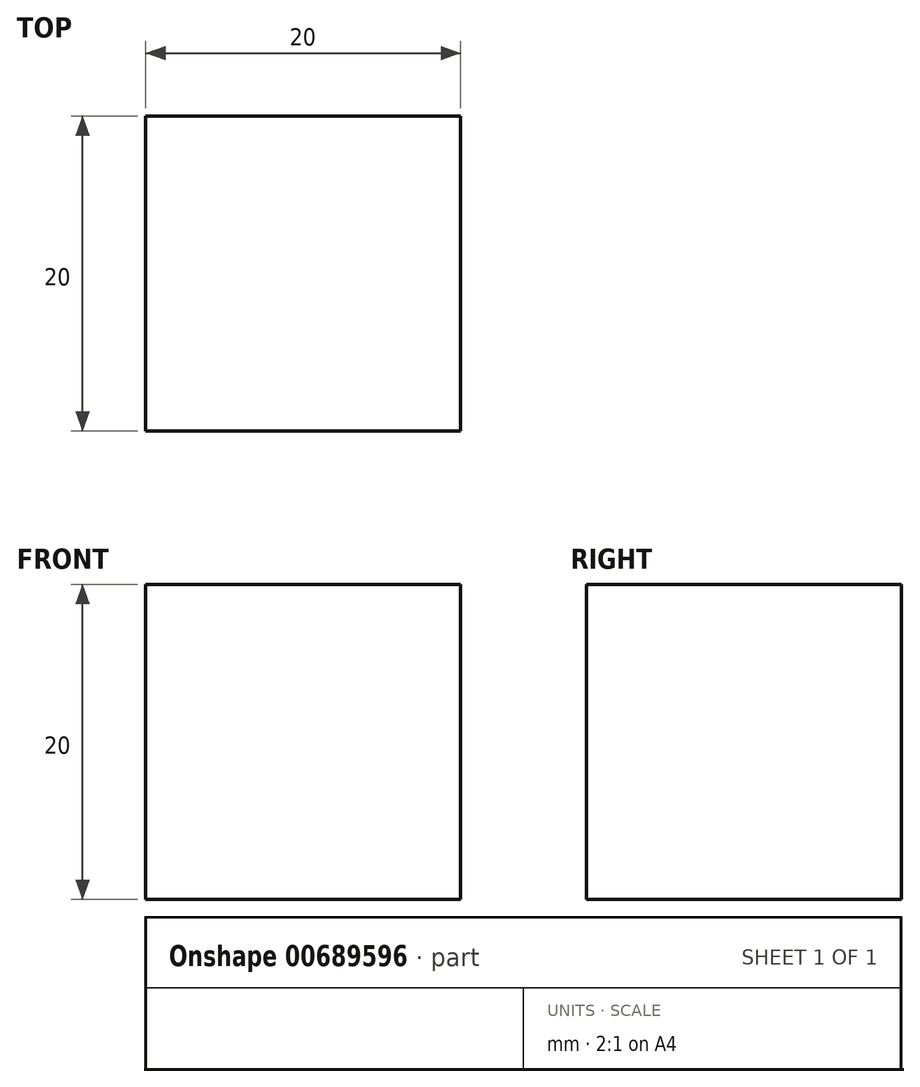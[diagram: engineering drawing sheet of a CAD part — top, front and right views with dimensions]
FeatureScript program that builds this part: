
annotation { "Feature Type Name" : "Feature", "Feature Type Description" : "" }
export const myFeature = defineFeature(function(context is Context, id is Id, definition is map)
    precondition{}
    {
        {
            var Q0;
            Q0=qCreatedBy(makeId("Top.planeOp"),FACE);
            var sketch = newSketch(context, id + "F0", { "sketchPlane" : qUnion([Q0])});
            skLineSegment(sketch, "E0.bottom", {"start": v(-10, 10) * mm, "end": v(10, 10) * mm});
            skLineSegment(sketch, "E0.top", {"start": v(-10, -10) * mm, "end": v(10, -10) * mm});
            skLineSegment(sketch, "E0.left", {"start": v(-10, 10) * mm, "end": v(-10, -10) * mm});
            skLineSegment(sketch, "E0.right", {"start": v(10, 10) * mm, "end": v(10, -10) * mm});
            skPoint(sketch, "E0.middle", {"position": v(0, 0) * mm});
            skSolve(sketch);
        }
        {
            var Q0;
            Q0 = qSketchRegion(id + "F0", true);
            extrude(context, id + "F1", {"entities" : qUnion([Q0]), "depth" : 20 * mm, "offsetDistance" : 25 * mm});
        }
    });
